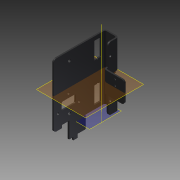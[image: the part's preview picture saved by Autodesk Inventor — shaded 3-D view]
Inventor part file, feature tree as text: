
AUTODESK INVENTOR PART (.ipt)
format: ipt  version: 2015 (Build 190159000, 159)  size: 478,208 bytes
history: native  units: mm
features: hole x11, extrude x10, fillet x5, other x3, plane x1
ambient origin geometry x8: Origin, YZ Plane, XZ Plane, XY Plane, X Axis, Y Axis, Z Axis, Center Point
bodies: Solid1 (feature_tree)
feature tree (30):
  extrude  "Extrusión1"  Depth=2.0mm
  fillet  "Empalme1"  Radius=2.0mm
  extrude  "Extrusión2"  Depth=2.0mm
  hole  "Agujero2"  [1 undecoded]
  extrude  "Extrusión4"  Depth=9.748846mm TaperAngle=0.0deg
  fillet  "Empalme3"  Radius=4.0mm
  hole  "Agujero5"  [1 undecoded]
  hole  "Agujero6"  [1 undecoded]
  other  "Eje de trabajo1"
  hole  "Agujero8"  [1 undecoded]
  hole  "Agujero9"  [1 undecoded]
  extrude  "Extrusión6"  Depth=12.5mm
  extrude  "Extrusión8"  Depth=75.0mm
  hole  "Agujero11"  [1 undecoded]
  fillet  "Empalme4"  Radius=3.0mm
  other  "Desplazar cara1"
  extrude  "Extrusión11"  Depth=20.0mm
  fillet  "Redondeo de esquina1"  Radius=3.0mm
  hole  "Agujero12"  [1 undecoded]
  extrude  "Extrusión13"  Depth=15.0mm
  plane  "Plano de trabajo1"
  extrude  "Extrusión14"  Depth=20.0mm
  extrude  "Extrusión15"  Depth=8.0mm
  hole  "Agujero13"  [1 undecoded]
  fillet  "Empalme6"  Radius=50.0mm
  hole  "Agujero14"  [1 undecoded]
  hole  "Agujero15"  [1 undecoded]
  hole  "Agujero16"  [1 undecoded]
  extrude  "Extrusión12"  Depth=50.0mm
  other  "Definición1"
note: 11 required parameter values undecoded (feature->parameter linkage not recoverable at this tier; creation-order binding heuristic only, values carry confidence <= 0.55)
